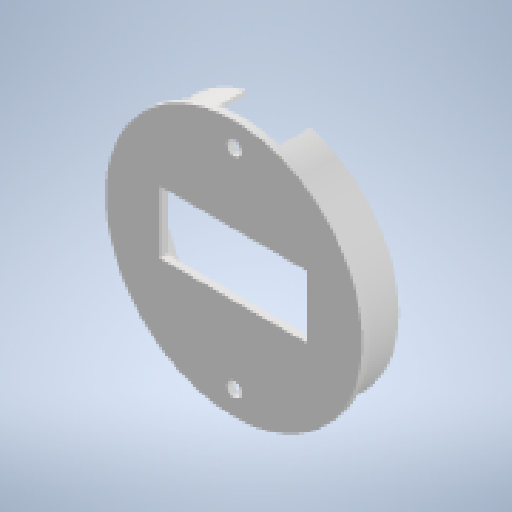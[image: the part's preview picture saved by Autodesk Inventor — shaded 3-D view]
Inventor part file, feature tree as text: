
AUTODESK INVENTOR PART (.ipt)
format: ipt  version: 2025.3 (Build 293356000, 356)  size: 157,184 bytes
history: native  units: in
note: dims shown in document units (in); Inventor stores cm internally (conversion verified against a paired STEP export)
features: reference x5, other x3, extrude x2, sketch x2, plane x1
ambient origin geometry x8: Origin, YZ Plane, XZ Plane, XY Plane, X Axis, Y Axis, Z Axis, Center Point
bodies: Solid1 (feature_tree)
feature tree (13):
  extrude  "Extrusion1"  Depth=0.3937in
  plane  "Work Plane1"
  extrude  "Extrusion2"  Depth=1.5748in
  sketch  "Sketch1"  dims[d2=0.3937in d3=0.0in d4=0.1575in]
  reference  "Reference1"
  reference  "Reference2"
  sketch  "Sketch2"  dims[d5=0.1575in d6=0.7874in d7=1.7717in d15=0.0787in d16=0.0in d32=0.6693in d33=1.5748in d36=0.0394in d37=0.0394in]
  reference  "Reference3"
  reference  "Reference4"
  reference  "Reference5"
  parser-record x1  (decoder bookkeeping rows leaked as tree rows — omitted from the tree; the rows remain in map.json)
  other  "Assembly1.iam"
  other  "main_body:1"
note: 1 file-system path scrubbed to <path> (originals preserved in map.json)
